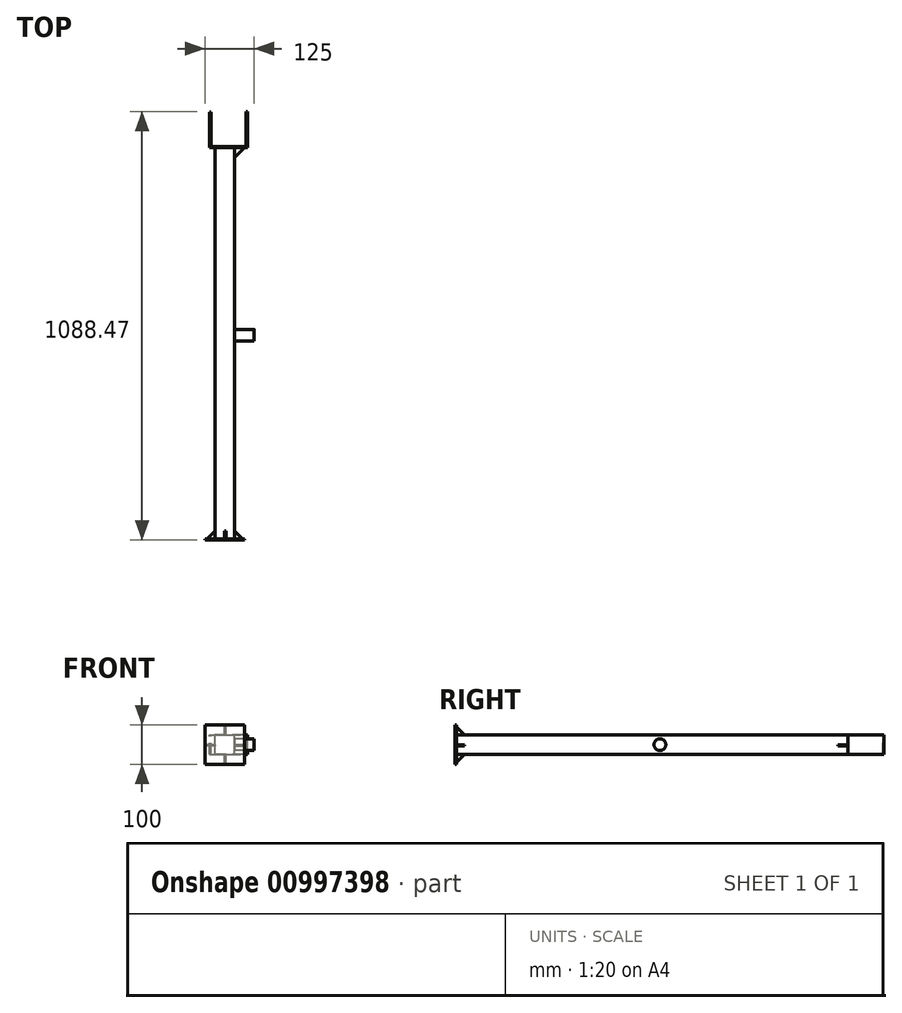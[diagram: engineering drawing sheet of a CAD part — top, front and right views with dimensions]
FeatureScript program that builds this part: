
annotation { "Feature Type Name" : "Feature", "Feature Type Description" : "" }
export const myFeature = defineFeature(function(context is Context, id is Id, definition is map)
    precondition{}
    {
        {
            var Q0;
            Q0=qCreatedBy(makeId("Front.planeOp"),FACE);
            var sketch = newSketch(context, id + "F0", { "sketchPlane" : qUnion([Q0])});
            skLineSegment(sketch, "E0.bottom", {"start": v(-25, -25) * mm, "end": v(25, -25) * mm});
            skLineSegment(sketch, "E0.top", {"start": v(-25, 25) * mm, "end": v(25, 25) * mm});
            skLineSegment(sketch, "E0.left", {"start": v(-25, -25) * mm, "end": v(-25, 25) * mm});
            skLineSegment(sketch, "E0.right", {"start": v(25, -25) * mm, "end": v(25, 25) * mm});
            skPoint(sketch, "E0.middle", {"position": v(0, 0) * mm});
            skSolve(sketch);
        }
        {
            var Q0;
            Q0 = qSketchRegion(id + "F0", true);
            extrude(context, id + "F1", {"entities" : qUnion([Q0]), "depth" : 994 * mm, "offsetDistance" : 25 * mm});
        }
        {
            var Q0;
            Q0=makeQuery(id+"F1.opExtrude","CAP_FACE",FACE,{"disambiguationData":[OSD([sQuery(id+"F0.wireOp",EDGE,"E0.bottom"),sQuery(id+"F0.wireOp",EDGE,"E0.top"),sQuery(id+"F0.wireOp",EDGE,"E0.left"),sQuery(id+"F0.wireOp",EDGE,"E0.right")])],"isStart":false});
            cPlane(context, id + "F2", {"entities" : qUnion([Q0]), "cplaneType" : CPlaneType.OFFSET, "offset" : 0 * mm, "width" : 150 * mm, "height" : 150 * mm});
        }
        {
            var Q0;
            Q0=qCreatedBy(id+"F2.planeOp",FACE);
            var sketch = newSketch(context, id + "F3", { "sketchPlane" : qUnion([Q0])});
            skLineSegment(sketch, "E1.bottom", {"start": v(-50, -50) * mm, "end": v(50, -50) * mm});
            skLineSegment(sketch, "E1.top", {"start": v(-50, 50) * mm, "end": v(50, 50) * mm});
            skLineSegment(sketch, "E1.left", {"start": v(-50, -50) * mm, "end": v(-50, 50) * mm});
            skLineSegment(sketch, "E1.right", {"start": v(50, -50) * mm, "end": v(50, 50) * mm});
            skPoint(sketch, "E1.middle", {"position": v(0, 0) * mm});
            skSolve(sketch);
        }
        {
            var Q0;
            Q0=makeQuery(id+"F3.imprint","IMPRINT",FACE,{"disambiguationData":[TD([[makeQuery(id+"F3.imprint","IMPRINT",EDGE,{"derivedFrom":sQuery(id+"F3.wireOp",EDGE,"E1.bottom")}),1.0]])]});
            extrude(context, id + "F4", {"entities" : qUnion([Q0]), "operationType" : NewBodyOperationType.ADD, "depth" : 3 * mm, "offsetDistance" : 25 * mm});
        }
        {
            var Q0;
            Q0=makeQuery(id+"F1.opExtrude","SWEPT_FACE",FACE,{"disambiguationData":[OSD([sQuery(id+"F0.wireOp",EDGE,"E0.top")])]});
            cPlane(context, id + "F5", {"entities" : qUnion([Q0]), "cplaneType" : CPlaneType.OFFSET, "offset" : 28 * mm, "oppositeDirection" : true, "width" : 150 * mm, "height" : 150 * mm});
        }
        {
            var Q0;
            Q0=qCreatedBy(id+"F5.planeOp",FACE);
            var sketch = newSketch(context, id + "F6", { "sketchPlane" : qUnion([Q0])});
            skLineSegment(sketch, "E2", {"start": v(25, -974) * mm, "end": v(25, -994) * mm});
            skLineSegment(sketch, "E3", {"start": v(25, -994) * mm, "end": v(45, -994) * mm});
            skLineSegment(sketch, "E4", {"start": v(45, -994) * mm, "end": v(25, -974) * mm});
            skLineSegment(sketch, "E5", {"start": v(-25, -974) * mm, "end": v(-25, -994) * mm});
            skLineSegment(sketch, "E6", {"start": v(-25, -994) * mm, "end": v(-45, -994) * mm});
            skLineSegment(sketch, "E7", {"start": v(-45, -994) * mm, "end": v(-25, -974) * mm});
            skSolve(sketch);
        }
        {
            var Q0;
            Q0=makeQuery(id+"F6.imprint","IMPRINT",FACE,{"disambiguationData":[TD([[makeQuery(id+"F6.imprint","IMPRINT",EDGE,{"derivedFrom":sQuery(id+"F6.wireOp",EDGE,"E5")}),-1.0]])]});
            var Q1;
            Q1=makeQuery(id+"F6.imprint","IMPRINT",FACE,{"disambiguationData":[TD([[makeQuery(id+"F6.imprint","IMPRINT",EDGE,{"derivedFrom":sQuery(id+"F6.wireOp",EDGE,"E2")}),1.0]])]});
            extrude(context, id + "F7", {"entities" : qUnion([Q0, Q1]), "operationType" : NewBodyOperationType.ADD, "depth" : 3 * mm, "offsetDistance" : 25 * mm});
        }
        {
            var Q0;
            Q0=makeQuery(id+"F1.opExtrude","SWEPT_FACE",FACE,{"disambiguationData":[OSD([sQuery(id+"F0.wireOp",EDGE,"E0.left")])]});
            cPlane(context, id + "F8", {"entities" : qUnion([Q0]), "cplaneType" : CPlaneType.OFFSET, "offset" : 28 * mm, "oppositeDirection" : true, "width" : 150 * mm, "height" : 150 * mm});
        }
        {
            var Q0;
            Q0=qCreatedBy(id+"F8.planeOp",FACE);
            var sketch = newSketch(context, id + "F9", { "sketchPlane" : qUnion([Q0])});
            skLineSegment(sketch, "E8", {"start": v(994, 25) * mm, "end": v(994, 45) * mm});
            skLineSegment(sketch, "E9", {"start": v(994, 45) * mm, "end": v(974, 25) * mm});
            skLineSegment(sketch, "E10", {"start": v(974, 25) * mm, "end": v(994, 25) * mm});
            skLineSegment(sketch, "E11", {"start": v(994, -25) * mm, "end": v(974, -25) * mm});
            skLineSegment(sketch, "E12", {"start": v(974, -25) * mm, "end": v(994, -45) * mm});
            skLineSegment(sketch, "E13", {"start": v(994, -45) * mm, "end": v(994, -25) * mm});
            skSolve(sketch);
        }
        {
            var Q0;
            Q0 = qSketchRegion(id + "F9", true);
            extrude(context, id + "F10", {"entities" : qUnion([Q0]), "operationType" : NewBodyOperationType.ADD, "depth" : 3 * mm, "offsetDistance" : 25 * mm});
        }
        {
            var Q0;
            Q0=makeQuery(id+"F1.opExtrude","SWEPT_FACE",FACE,{"disambiguationData":[OSD([sQuery(id+"F0.wireOp",EDGE,"E0.top")])]});
            cPlane(context, id + "F11", {"entities" : qUnion([Q0]), "cplaneType" : CPlaneType.OFFSET, "offset" : 0 * mm, "width" : 150 * mm, "height" : 150 * mm});
        }
        {
            var Q0;
            Q0=qCreatedBy(id+"F11.planeOp",FACE);
            var sketch = newSketch(context, id + "F12", { "sketchPlane" : qUnion([Q0])});
            skLineSegment(sketch, "E14.top", {"start": v(58, 0) * mm, "end": v(-38, 0) * mm});
            skLineSegment(sketch, "E14.right", {"start": v(-38, 90) * mm, "end": v(-38, 0) * mm});
            skPoint(sketch, "E14.middle", {"position": v(0, 45) * mm});
            skLineSegment(sketch, "E15", {"start": v(-38, 90) * mm, "end": v(-35, 90) * mm});
            skLineSegment(sketch, "E16", {"start": v(-35, 90) * mm, "end": v(-35, 3) * mm});
            skPoint(sketch, "E17.start.orphan", {"position": v(68.35, 90) * mm});
            skPoint(sketch, "E14.left.start.orphan", {"position": v(38, 90) * mm});
            skPoint(sketch, "E18.orphan", {"position": v(38, 0) * mm});
            skLineSegment(sketch, "E19", {"start": v(-35, 3) * mm, "end": v(55, 3) * mm});
            skLineSegment(sketch, "E20", {"start": v(55, 3) * mm, "end": v(55, 91.47) * mm});
            skLineSegment(sketch, "E21", {"start": v(55, 91.47) * mm, "end": v(58, 91.47) * mm});
            skLineSegment(sketch, "E22", {"start": v(58, 91.47) * mm, "end": v(58, 0) * mm});
            skSolve(sketch);
        }
        {
            var Q0;
            Q0 = qSketchRegion(id + "F12", true);
            extrude(context, id + "F13", {"entities" : qUnion([Q0]), "oppositeDirection" : true, "depth" : 50 * mm, "offsetDistance" : 25 * mm});
        }
        {
            var Q0;
            Q0=qCreatedBy(id+"F5.planeOp",FACE);
            var sketch = newSketch(context, id + "F14", { "sketchPlane" : qUnion([Q0])});
            skLineSegment(sketch, "E23", {"start": v(25, -25) * mm, "end": v(25, 0) * mm});
            skLineSegment(sketch, "E24", {"start": v(25, 0) * mm, "end": v(50, 0) * mm});
            skLineSegment(sketch, "E25", {"start": v(50, 0) * mm, "end": v(25, -25) * mm});
            skSolve(sketch);
        }
        {
            var Q0;
            Q0 = qSketchRegion(id + "F14", true);
            extrude(context, id + "F15", {"entities" : qUnion([Q0]), "depth" : 3 * mm, "offsetDistance" : 25 * mm});
        }
        {
            var Q0;
            Q0=makeQuery(id+"F1.opExtrude","SWEPT_FACE",FACE,{"disambiguationData":[OSD([sQuery(id+"F0.wireOp",EDGE,"E0.right")])]});
            cPlane(context, id + "F16", {"entities" : qUnion([Q0]), "cplaneType" : CPlaneType.OFFSET, "offset" : 0 * mm, "width" : 150 * mm, "height" : 150 * mm});
        }
        {
            var Q0;
            Q0=qCreatedBy(id+"F16.planeOp",FACE);
            var sketch = newSketch(context, id + "F17", { "sketchPlane" : qUnion([Q0])});
            skCircle(sketch, "E26", {"center": v(-477, 0) * mm, "radius": 15 * mm});
            skSolve(sketch);
        }
        {
            var Q0;
            Q0 = qSketchRegion(id + "F17", true);
            extrude(context, id + "F18", {"entities" : qUnion([Q0]), "operationType" : NewBodyOperationType.ADD, "depth" : 50 * mm, "offsetDistance" : 25 * mm});
        }
    });
